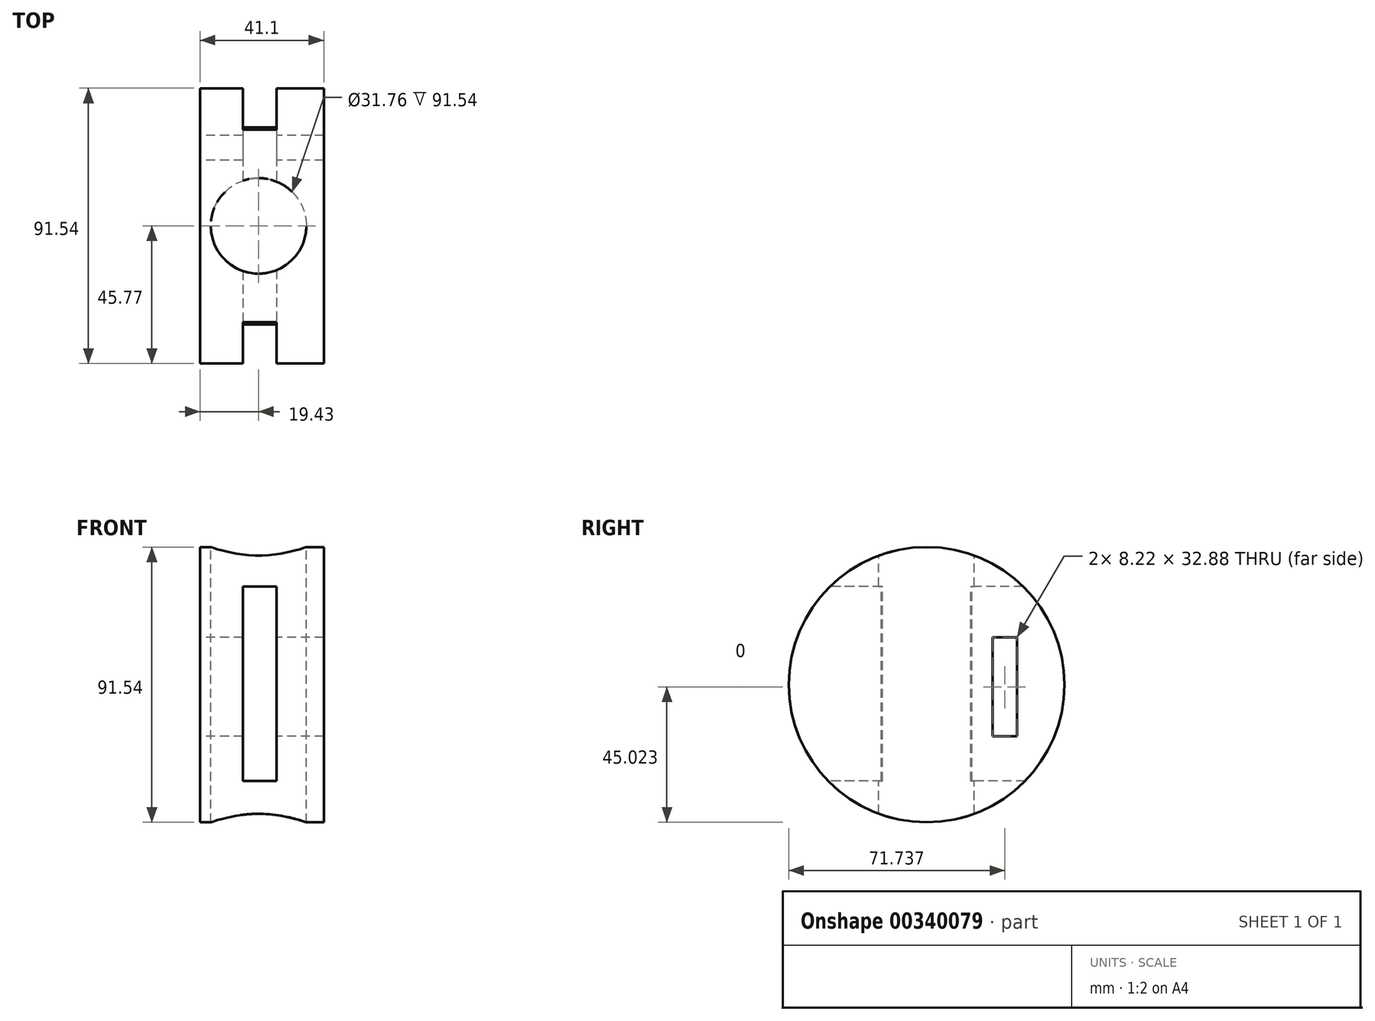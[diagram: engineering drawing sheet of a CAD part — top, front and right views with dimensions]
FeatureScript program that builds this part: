
annotation { "Feature Type Name" : "Feature", "Feature Type Description" : "" }
export const myFeature = defineFeature(function(context is Context, id is Id, definition is map)
    precondition{}
    {
        {
            var Q0;
            Q0=qCreatedBy(makeId("Top.planeOp"),FACE);
            var sketch = newSketch(context, id + "F0", { "sketchPlane" : qUnion([Q0])});
            skLineSegment(sketch, "E0.bottom", {"start": v(-19.43, 0) * mm, "end": v(21.67, 0) * mm});
            skLineSegment(sketch, "E0.top", {"start": v(-19.43, 45.77) * mm, "end": v(21.67, 45.77) * mm});
            skLineSegment(sketch, "E0.left", {"start": v(-19.43, 0) * mm, "end": v(-19.43, 45.77) * mm});
            skLineSegment(sketch, "E0.right", {"start": v(21.67, 0) * mm, "end": v(21.67, 45.77) * mm});
            skSolve(sketch);
        }
        {
            var Q0;
            Q0 = qSketchRegion(id + "F0", true);
            var Q1;
            Q1=sQuery(id+"F0.wireOp",EDGE,"E0.bottom");
            revolve(context, id + "F1", {"entities" : qUnion([Q0]), "axis" : qUnion([Q1]), "revolveType" : RevolveType.ONE_DIRECTION, "angle" : 360 * degree});
        }
        {
            var Q0;
            Q0=qCreatedBy(makeId("Right.planeOp"),FACE);
            var sketch = newSketch(context, id + "F2", { "sketchPlane" : qUnion([Q0])});
            skLineSegment(sketch, "E1.bottom", {"start": v(30.08, -17.19) * mm, "end": v(21.86, -17.19) * mm});
            skLineSegment(sketch, "E1.top", {"start": v(30.08, 15.7) * mm, "end": v(21.86, 15.7) * mm});
            skLineSegment(sketch, "E1.left", {"start": v(30.08, -17.19) * mm, "end": v(30.08, 15.7) * mm});
            skLineSegment(sketch, "E1.right", {"start": v(21.86, -17.19) * mm, "end": v(21.86, 15.7) * mm});
            skSolve(sketch);
        }
        {
            var Q0;
            Q0 = qSketchRegion(id + "F2", true);
            extrude(context, id + "F3", {"entities" : qUnion([Q0]), "operationType" : NewBodyOperationType.REMOVE, "endBound" : BoundingType.SYMMETRIC, "depth" : 45 * mm});
        }
        {
            var Q0;
            Q0=qCreatedBy(makeId("Front.planeOp"),FACE);
            var sketch = newSketch(context, id + "F4", { "sketchPlane" : qUnion([Q0])});
            skLineSegment(sketch, "E2.bottom", {"start": v(5.98, -31.94) * mm, "end": v(-5.23, -31.94) * mm});
            skLineSegment(sketch, "E2.top", {"start": v(5.98, 32.7) * mm, "end": v(-5.23, 32.7) * mm});
            skLineSegment(sketch, "E2.left", {"start": v(5.98, -31.94) * mm, "end": v(5.98, 32.7) * mm});
            skLineSegment(sketch, "E2.right", {"start": v(-5.23, -31.94) * mm, "end": v(-5.23, 32.7) * mm});
            skSolve(sketch);
        }
        {
            var Q0;
            Q0 = qSketchRegion(id + "F4", true);
            extrude(context, id + "F5", {"entities" : qUnion([Q0]), "operationType" : NewBodyOperationType.REMOVE, "endBound" : BoundingType.SYMMETRIC, "oppositeDirection" : true, "depth" : 100 * mm});
        }
        {
            var Q0;
            Q0=qCreatedBy(makeId("Top.planeOp"),FACE);
            var sketch = newSketch(context, id + "F6", { "sketchPlane" : qUnion([Q0])});
            skCircle(sketch, "E3", {"center": v(0, 0) * mm, "radius": 15.88 * mm});
            skSolve(sketch);
        }
        {
            var Q0;
            Q0 = qSketchRegion(id + "F6", true);
            extrude(context, id + "F7", {"entities" : qUnion([Q0]), "operationType" : NewBodyOperationType.REMOVE, "endBound" : BoundingType.SYMMETRIC, "oppositeDirection" : true, "depth" : 100 * mm});
        }
    });
